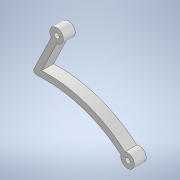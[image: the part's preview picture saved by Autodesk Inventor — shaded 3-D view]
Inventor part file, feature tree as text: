
AUTODESK INVENTOR PART (.ipt)
format: ipt  version: 2020 (Build 240168000, 168)  size: 176,128 bytes
history: native  units: mm
features: sketch x3, other x3, extrude x2, reference x2, projected_geometry x2, hole x1, fillet x1
ambient origin geometry x8: Origin, YZ Plane, XZ Plane, XY Plane, X Axis, Y Axis, Z Axis, Center Point
bodies: Solid1 (feature_tree)
feature tree (14):
  extrude  "Extrusion1"  Depth=27.0mm
  hole  "Hole1"  [1 undecoded]
  extrude  "Extrusion2"  Depth=2.0mm
  fillet  "Fillet1"  Radius=70.0mm
  sketch  "Sketch1"  dims[d0=8.0mm d1=27.0mm]
  reference  "Reference1"
  reference  "Reference2"
  sketch  "Sketch2"  dims[d3=8.0mm d4=3.5mm]
  projected_geometry  "Projected Loop1"
  sketch  "Sketch3"  dims[d6=3.5mm d7=70.0mm d8=70.0mm d9=7.0mm d10=0.0mm d11=3.0mm d12=6.0mm d13=4.0mm d14=2.0mm d15=90.0deg d16=8.0mm d17=0.0mm d18=8.0mm d19=8.0mm d20=2.0mm d21=0.0mm d22=2.0mm]
  projected_geometry  "Projected Loop2"
  parser-record x1  (decoder bookkeeping rows leaked as tree rows — omitted from the tree; the rows remain in map.json)
  other  "leg_1.iam"
  other  "leg_holder_2:1"
note: 1 required parameter value undecoded (feature->parameter linkage not recoverable at this tier; creation-order binding heuristic only, values carry confidence <= 0.55)
note: 1 file-system path scrubbed to <path> (originals preserved in map.json)
